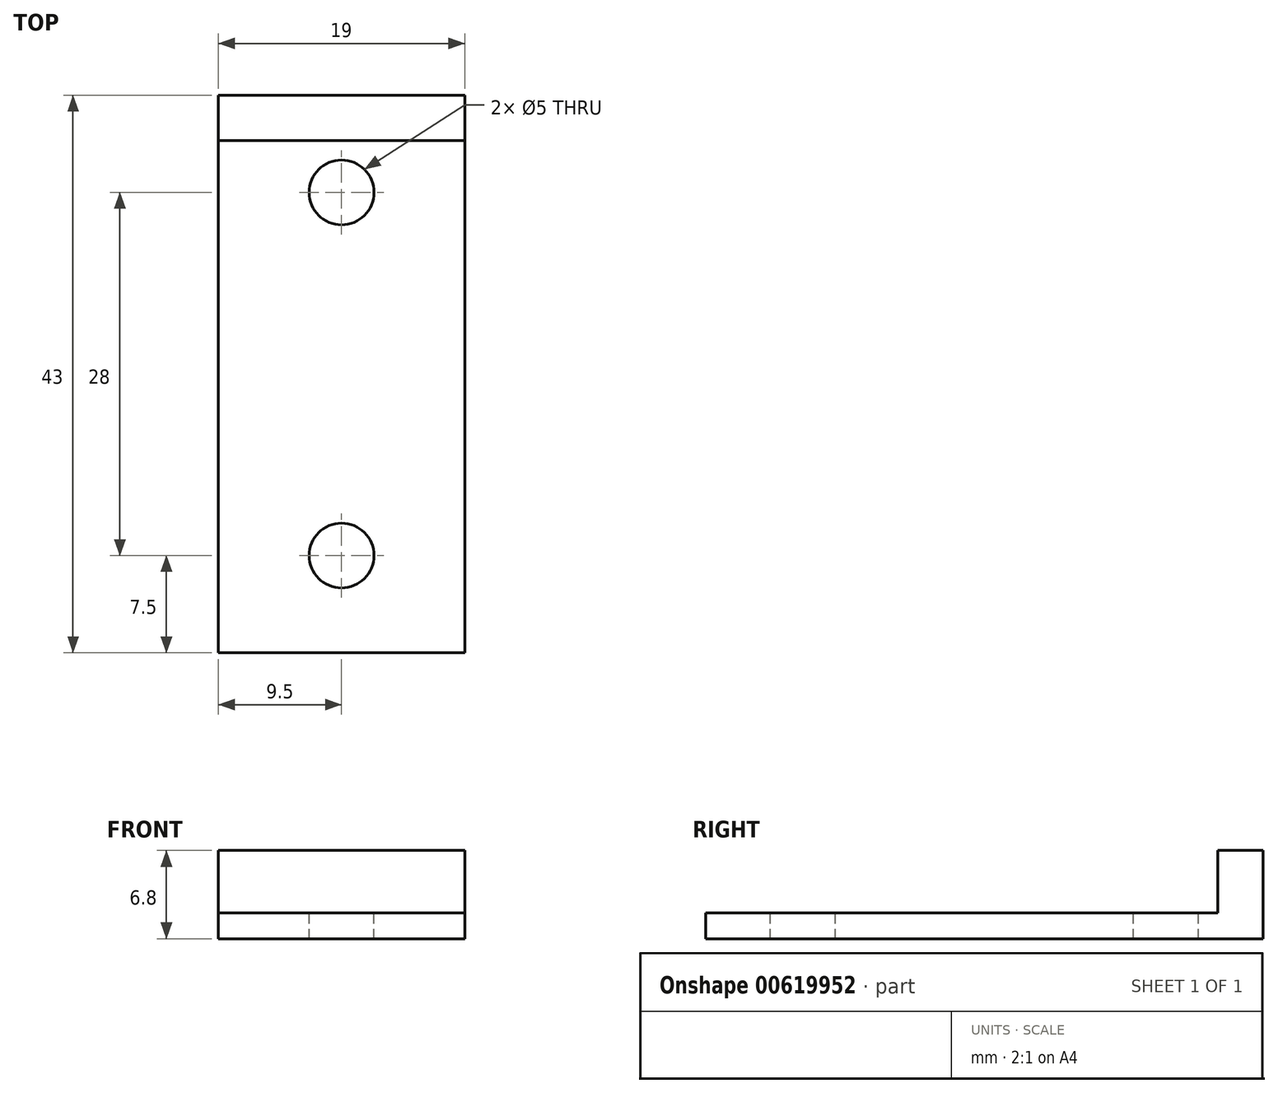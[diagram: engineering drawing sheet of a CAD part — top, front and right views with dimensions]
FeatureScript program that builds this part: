
annotation { "Feature Type Name" : "Feature", "Feature Type Description" : "" }
export const myFeature = defineFeature(function(context is Context, id is Id, definition is map)
    precondition{}
    {
        {
            var Q0;
            Q0=qCreatedBy(makeId("Right.planeOp"),FACE);
            var sketch = newSketch(context, id + "F0", { "sketchPlane" : qUnion([Q0])});
            skLineSegment(sketch, "E0.bottom", {"start": v(21.5, 1) * mm, "end": v(-21.5, 1) * mm});
            skLineSegment(sketch, "E0.top", {"start": v(21.5, -1) * mm, "end": v(-21.5, -1) * mm});
            skLineSegment(sketch, "E0.left", {"start": v(21.5, 1) * mm, "end": v(21.5, -1) * mm});
            skLineSegment(sketch, "E0.right", {"start": v(-21.5, 1) * mm, "end": v(-21.5, -1) * mm});
            skPoint(sketch, "E0.middle", {"position": v(0, 0) * mm});
            skPoint(sketch, "E1", {"position": v(-18, 1) * mm});
            skLineSegment(sketch, "E2", {"start": v(0, 0) * mm, "end": v(0, 11.73) * mm, "construction": true});
            skPoint(sketch, "E2.endSnap0", {"position": v(0, 1) * mm});
            skPoint(sketch, "E3.MirrorP", {"position": v(18, 1) * mm});
            skLineSegment(sketch, "E4.bottom", {"start": v(-18, 1) * mm, "end": v(-21.5, 1) * mm});
            skLineSegment(sketch, "E4.top", {"start": v(-18, 5.8) * mm, "end": v(-21.5, 5.8) * mm});
            skLineSegment(sketch, "E4.left", {"start": v(-18, 1) * mm, "end": v(-18, 5.8) * mm});
            skLineSegment(sketch, "E4.right", {"start": v(-21.5, 1) * mm, "end": v(-21.5, 5.8) * mm});
            skLineSegment(sketch, "E5.MirrorCS", {"start": v(18, 1) * mm, "end": v(18, 5.8) * mm});
            skLineSegment(sketch, "E6.MirrorCS", {"start": v(18, 5.8) * mm, "end": v(21.5, 5.8) * mm});
            skLineSegment(sketch, "E7.MirrorCS", {"start": v(21.5, 1) * mm, "end": v(21.5, 5.8) * mm});
            skSolve(sketch);
        }
        {
            var Q0;
            Q0=makeQuery(id+"F0.imprint","IMPRINT",FACE,{"disambiguationData":[TD([[makeQuery(id+"F0.imprint","IMPRINT",EDGE,{"derivedFrom":sQuery(id+"F0.wireOp",EDGE,"E4.bottom")}),-1.0]])]});
            var Q1;
            Q1=makeQuery(id+"F0.imprint","IMPRINT",FACE,{"disambiguationData":[TD([[makeQuery(id+"F0.imprint","IMPRINT",EDGE,{"derivedFrom":sQuery(id+"F0.wireOp",EDGE,"E0.top")}),-1.0]])]});
            var Q2;
            {var subQ2=sQuery(id+"F0.wireOp",EDGE,"E5.MirrorCS");Q2=makeQuery(id+"F0.imprint","IMPRINT",FACE,{"disambiguationData":[TD([[makeQuery(id+"F0.imprint","IMPRINT",EDGE,{"derivedFrom":subQ2}),-1.0]])]});}
            extrude(context, id + "F1", {"entities" : qUnion([Q0, Q1, Q2]), "depth" : 19 * mm, "offsetDistance" : 25 * mm});
        }
        {
            var Q0;
            Q0=makeQuery(id+"F1.opExtrude","SWEPT_FACE",FACE,{"disambiguationData":[OSD([sQuery(id+"F0.wireOp",EDGE,"E0.top")])]});
            var sketch = newSketch(context, id + "F2", { "sketchPlane" : qUnion([Q0])});
            skLineSegment(sketch, "E8", {"start": v(0, 0) * mm, "end": v(19, 0) * mm, "construction": true});
            skPoint(sketch, "E9", {"position": v(9.5, 14) * mm});
            skPoint(sketch, "E9.positionSnap0", {"position": v(9.5, 21.5) * mm});
            skPoint(sketch, "E10.MirrorP", {"position": v(9.5, -14) * mm});
            skSolve(sketch);
        }
        {
            var Q0;
            Q0=sQuery(id+"F2.wireOp",VERTEX,"E9");
            var Q1;
            Q1=sQuery(id+"F2.wireOp",VERTEX,"E10.MirrorP");
            var Q2;
            Q2=makeQuery(id+"F1.opExtrude","SWEPT_BODY",BODY,{"disambiguationData":[OSD([sQuery(id+"F0.wireOp",EDGE,"E0.bottom"),sQuery(id+"F0.wireOp",EDGE,"E0.top"),sQuery(id+"F0.wireOp",EDGE,"E0.left"),sQuery(id+"F0.wireOp",EDGE,"E0.right"),sQuery(id+"F0.wireOp",EDGE,"E4.top"),sQuery(id+"F0.wireOp",EDGE,"E4.left"),sQuery(id+"F0.wireOp",EDGE,"E4.right"),sQuery(id+"F0.wireOp",EDGE,"E5.MirrorCS"),sQuery(id+"F0.wireOp",EDGE,"E6.MirrorCS"),sQuery(id+"F0.wireOp",EDGE,"E7.MirrorCS")])]});
            hole(context, id + "F3", {"style" : HoleStyle.SIMPLE, "endStyle" : HoleEndStyle.BLIND, "standardTappedOrClearance" : lookupTablePath({ "standard" : "ISO", "size" : "5", "type" : "Drilled" }), "standardBlindInLast" : lookupTablePath({ "standard" : "ISO", "size" : "5", "type" : "Drilled" }), "holeDiameter" : 5 * mm, "majorDiameter" : 5 * mm, "holeDepth" : 10 * mm, "isTappedThrough" : true, "tappedDepth" : 7.6 * mm, "tapClearance" : 3, "locations" : qUnion([Q0, Q1]), "scope" : qUnion([Q2]), "startStyle" : HoleStartStyle.SKETCH});
        }
    });
